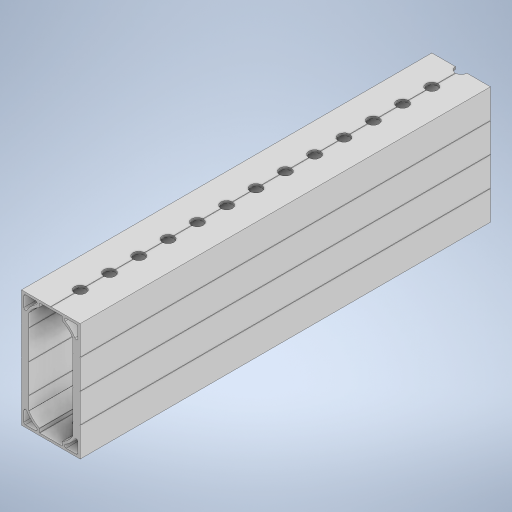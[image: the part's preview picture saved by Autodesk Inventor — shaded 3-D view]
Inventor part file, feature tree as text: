
AUTODESK INVENTOR PART (.ipt)
format: ipt  version: 2023.4 (Build 274418000, 418)  size: 740,352 bytes
history: native  units: in
note: dims shown in document units (in); Inventor stores cm internally (conversion verified against a paired STEP export)
features: extrude x1, sketch x1, other x1
ambient origin geometry x8: Origin, YZ Plane, XZ Plane, XY Plane, X Axis, Y Axis, Z Axis, Center Point
bodies: Solid1 (feature_tree)
feature tree (3):
  extrude  "Extrusion1"  [1 undecoded]
  sketch  "Sketch1"  dims[d0=40.0in d1=0.0in]
  other  "Internal Fillets"
note: 1 required parameter value undecoded (feature->parameter linkage not recoverable at this tier; creation-order binding heuristic only, values carry confidence <= 0.55)
